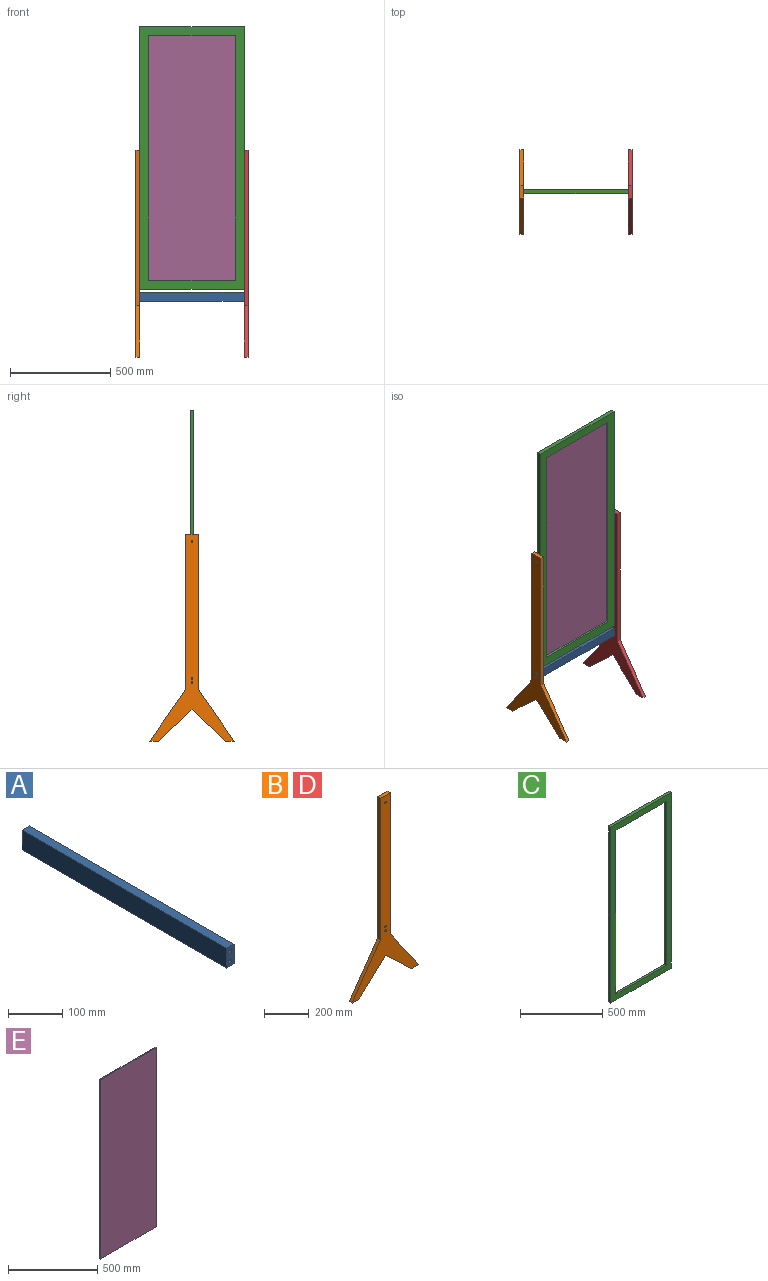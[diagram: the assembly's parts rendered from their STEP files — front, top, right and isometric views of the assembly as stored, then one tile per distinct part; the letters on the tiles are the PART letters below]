
ASSEMBLY  parts=5 mates=4
PART A: 14 faces, bbox 19.1x533.4x44.5 mm
  f0: plane 533.4x44.45mm, normal (1,0,0), area 23709.6mm2, adj f1,f3,f4,f5
  f1: plane 533.4x19.05mm, normal (0,0,1), area 10161.3mm2, adj f0,f2,f4,f5
  f2: plane 533.4x44.45mm, normal (-1,0,0), area 23709.6mm2, adj f1,f3,f4,f5
  f3: plane 533.4x19.05mm, normal (0,0,-1), area 10161.3mm2, adj f0,f2,f4,f5
  f4: plane 44.45x19.05mm, normal (0,1,0), area 704.3mm2, adj f0,f1,f2,f3,f10,f12
  f5: plane 44.45x19.05mm, normal (0,-1,0), area 704.3mm2, adj f0,f1,f2,f3,f6,f8
  f6: cylinder r=4.76mm len=25.4mm, axis (0,-1,0), area 760.1mm2, adj f5,f7
  f7: plane 9.53x9.53mm, normal (0,-1,0), area 71.3mm2, adj f6
  f8: cylinder r=4.76mm len=25.4mm, axis (0,-1,0), area 760.1mm2, adj f5,f9
  f9: plane 9.53x9.53mm, normal (0,-1,0), area 71.3mm2, adj f8
  f10: cylinder r=4.76mm len=25.4mm, axis (0,1,0), area 760.1mm2, adj f4,f11
  f11: plane 9.53x9.53mm, normal (0,1,0), area 71.3mm2, adj f10
  f12: cylinder r=4.76mm len=25.4mm, axis (0,1,0), area 760.1mm2, adj f4,f13
  f13: plane 9.53x9.53mm, normal (0,1,0), area 71.3mm2, adj f12
PART B: 14 faces, bbox 421.7x19.1x1032.3 mm
  f0: plane 257.64x179.1mm, normal (-0.82,0,0.57), area 5977.5mm2, adj f1,f6,f7,f8
  f1: plane 44.45x19.05mm, normal (0,0,-1), area 846.8mm2, adj f0,f2,f6,f7
  f2: plane 166.4x156.75mm, normal (0.69,0,-0.73), area 4354.8mm2, adj f1,f3,f6,f7
  f3: plane 166.4x156.75mm, normal (-0.69,0,-0.73), area 4354.8mm2, adj f2,f4,f6,f7
  f4: plane 44.45x19.05mm, normal (0,0,-1), area 846.8mm2, adj f3,f5,f6,f7
  f5: plane 257.64x179.1mm, normal (0.82,0,0.57), area 5977.5mm2, adj f4,f6,f7,f9
  f6: plane 1032.34x421.69mm, normal (0,-1,0), area 85400.9mm2, adj f0,f1,f2,f3,f4,f5,f8,f9
  f7: plane 1032.34x421.69mm, normal (0,1,0), area 85400.9mm2, adj f0,f1,f2,f3,f4,f5,f8,f9
  f8: plane 774.7x19.05mm, normal (-1,0,0), area 14758mm2, adj f0,f6,f7,f10
  f9: plane 774.7x19.05mm, normal (1,0,0), area 14758mm2, adj f5,f6,f7,f10
  f10: plane 63.5x19.05mm, normal (0,0,1), area 1209.7mm2, adj f6,f7,f8,f9
  f11: cylinder r=4.76mm len=19.05mm, axis (0,1,0), area 570mm2, adj f6,f7
  f12: cylinder r=4.76mm len=19.05mm, axis (0,1,0), area 570mm2, adj f6,f7
  f13: cylinder r=4.76mm len=19.05mm, axis (0,1,0), area 570mm2, adj f6,f7
PART C: 19 faces, bbox 520.7x19.1x1308.1 mm
  f0: plane 431.8x12.7mm, normal (0,0,-1), area 5483.9mm2, adj f1,f3,f9,f14
  f1: plane 1219.2x12.7mm, normal (-1,0,0), area 15483.8mm2, adj f0,f2,f9,f14
  f2: plane 431.8x12.7mm, normal (0,0,1), area 5483.9mm2, adj f1,f3,f9,f14
  f3: plane 1219.2x12.7mm, normal (1,0,0), area 15483.8mm2, adj f0,f2,f9,f14
  f4: plane 1308.1x520.7mm, normal (0,1,0), area 133548.2mm2, adj f5,f6,f7,f8,f10,f11,f12,f13
  f5: plane 520.7x19.05mm, normal (0,0,-1), area 9919.3mm2, adj f4,f6,f8,f9
  f6: plane 1308.1x19.05mm, normal (1,0,0), area 24848mm2, adj f4,f5,f7,f9,f17
  f7: plane 520.7x19.05mm, normal (0,0,1), area 9919.3mm2, adj f4,f6,f8,f9
  f8: plane 1308.1x19.05mm, normal (-1,0,0), area 24848mm2, adj f4,f5,f7,f9,f15
  f9: plane 1308.1x520.7mm, normal (0,-1,0), area 154677.1mm2, adj f0,f1,f2,f3,f5,f6,f7,f8
  f10: plane 1231.9x6.35mm, normal (1,0,0), area 7822.6mm2, adj f4,f11,f13,f14
  f11: plane 444.5x6.35mm, normal (0,0,-1), area 2822.6mm2, adj f4,f10,f12,f14
  f12: plane 1231.9x6.35mm, normal (-1,0,0), area 7822.6mm2, adj f4,f11,f13,f14
  f13: plane 444.5x6.35mm, normal (0,0,1), area 2822.6mm2, adj f4,f10,f12,f14
  f14: plane 1231.9x444.5mm, normal (0,1,0), area 21128.9mm2, adj f0,f1,f2,f3,f10,f11,f12,f13
  f15: cylinder r=4.76mm len=25.4mm, axis (-1,0,0), area 760.1mm2, adj f8,f16
  f16: plane 9.53x9.53mm, normal (-1,0,0), area 71.3mm2, adj f15
  f17: cylinder r=4.76mm len=25.4mm, axis (1,0,0), area 760.1mm2, adj f6,f18
  f18: plane 9.53x9.53mm, normal (1,0,0), area 71.3mm2, adj f17
PART D: same geometry as B
PART E: 6 faces, bbox 444.5x6.4x1231.9 mm
  f0: plane 1231.9x6.35mm, normal (-1,0,0), area 7822.6mm2, adj f1,f3,f4,f5
  f1: plane 444.5x6.35mm, normal (0,0,1), area 2822.6mm2, adj f0,f2,f4,f5
  f2: plane 1231.9x6.35mm, normal (1,0,0), area 7822.6mm2, adj f1,f3,f4,f5
  f3: plane 444.5x6.35mm, normal (0,0,-1), area 2822.6mm2, adj f0,f2,f4,f5
  f4: plane 1231.9x444.5mm, normal (0,1,0), area 547579.5mm2, adj f0,f1,f2,f3
  f5: plane 1231.9x444.5mm, normal (0,-1,0), area 547579.5mm2, adj f0,f1,f2,f3
PLACE A rot(axis=(0,0,-1),90deg) t=(285.1,697.19,-290.11)mm
PLACE B rot(axis=(0,0,-1),90deg) t=(297.8,697.19,-334.94)mm
PLACE C t=(558.15,706.71,401.66)mm
PLACE D rot(axis=(0,0,-1),90deg) t=(837.55,697.19,-334.94)mm
PLACE E t=(558.15,706.71,401.66)mm
MATE fastened E.f1 <-> C.f11  axis (0,0,1) through (558.15,703.54,1017.61)mm
MATE revolute B.f13 <-> C.f15  axis (1,0,0) through (297.8,697.19,401.66)mm
MATE fastened A.f8 <-> D.f11  axis (1,0,0) through (818.5,697.19,-278.98)mm
MATE revolute C.f17 <-> D.f13  axis (1,0,0) through (818.5,697.19,401.66)mm
